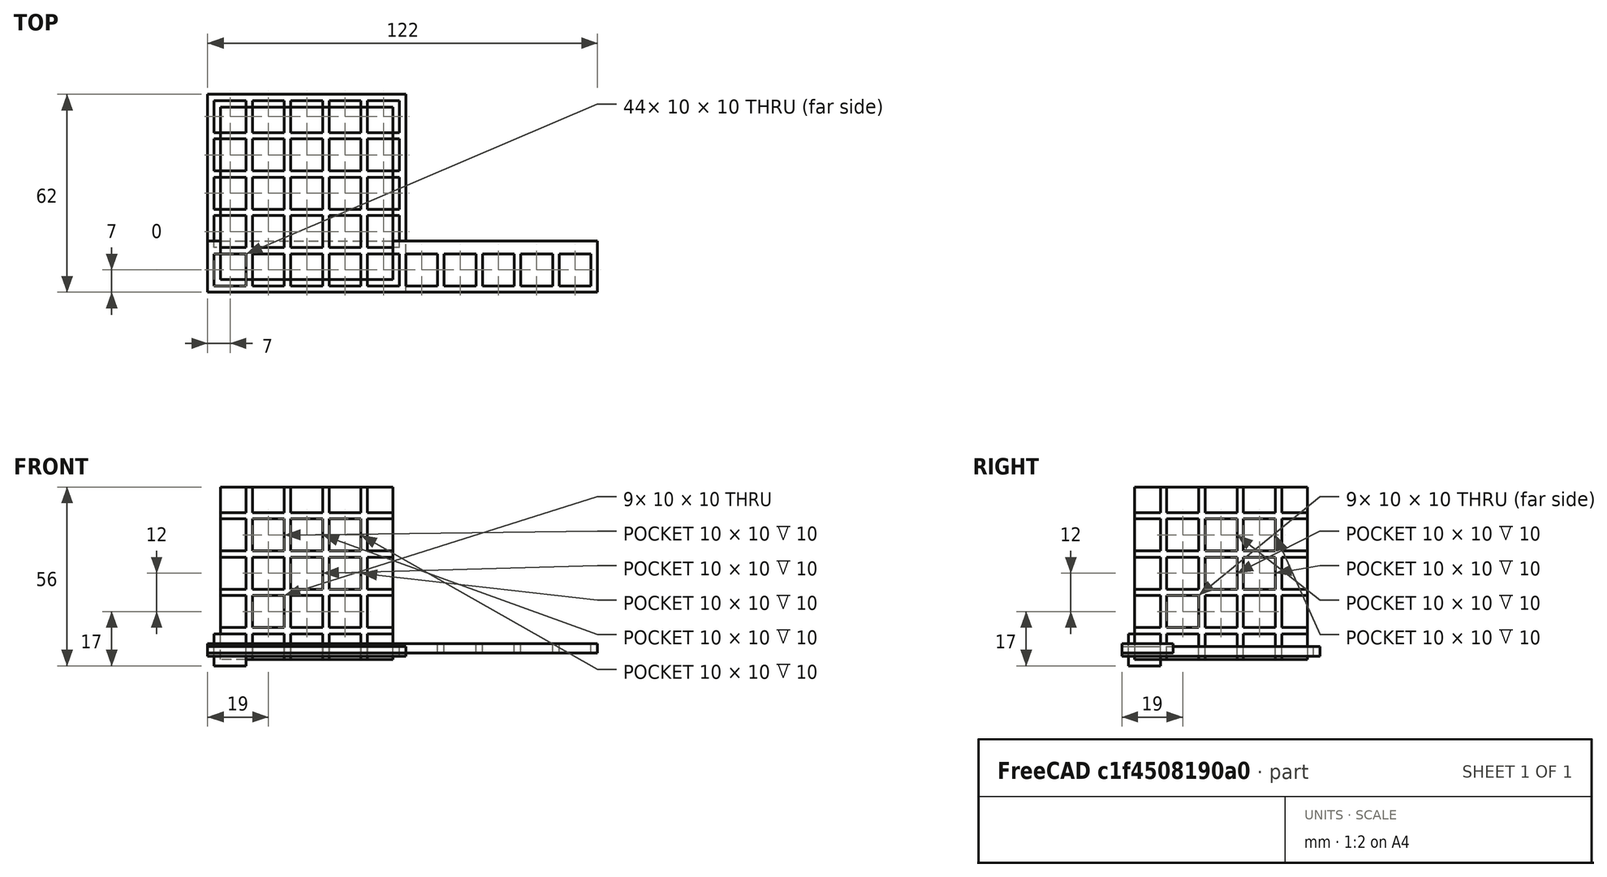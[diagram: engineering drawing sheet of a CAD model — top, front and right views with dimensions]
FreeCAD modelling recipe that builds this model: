
FCSTD DOCUMENT  (FreeCAD 0.20R29177 (Git))
Label: Video10
License: All rights reserved
LicenseURL: http://en.wikipedia.org/wiki/All_rights_reserved
objects: Part::Box×6, Part::FeaturePython×3, Part::Cut×3
note: 9 computed .brp shape members not serialized (recipe doc carries the construction recipe); baked Part::Feature solids carry a one-line shape summary decoded from their .brp

FEATURE [Part::Box] Box  label="master_box"
  AttacherType = Attacher::AttachEngine3D
  Height = 10
  Length = 10
  Width = 10
FEATURE [Part::FeaturePython] Array  # Draft array (typed FeaturePython)
  AlwaysSyncPlacement = false
  Angle = 360
  ArrayType = 0
  Axis = (0,0,1)
  Base = -> Box
  Center = (0,0,0)
  Count = 20
  ExpandArray = false
  Fuse = false
  IntervalAxis = (0,0,0)
  IntervalX = (12,0,0)
  IntervalY = (0,0,0)
  IntervalZ = (0,0,100)
  NumberCircles = 3
  NumberPolar = 5
  NumberX = 10
  NumberY = 2
  NumberZ = 1
  PlacementList = 20 placements: [(0,0,0),(0,0,0),(12,0,0),(12,0,0),(24,0,0),(24,0,0),(36,0,0),(36,0,0),(48,0,0),(48,0,0),(60,0,0),(60,0,0),(72,0,0),(72,0,0),(84,0,0),(84,0,0),(96,0,0),(96,0,0),(108,0,0),(108,0,0)]
  RadialDistance = 50
  ScaleList = (20) [(1,1,1),(1,1,1),(1,1,1),(1,1,1),(1,1,1),(1,1,1),(1,1,1),(1,1,1),(1,1,1),(1,1,1),(1,1,1),(1,1,1),(1,1,1),(1,1,1),(1,1,1),(1,1,1),(1,1,1),(1,1,1),+2 more]
  Symmetry = 1
  TangentialDistance = 25
FEATURE [Part::Box] Box001  label="Cubo"
  AttacherType = Attacher::AttachEngine3D
  Height = 3
  Length = 122
  Placement = pos=(-2,-2,4) rot=(0,0,1;0rad)
  Width = 16
FEATURE [Part::Cut] Cut
  Base = -> Box001
  Tool = -> Array
FEATURE [Part::Box] Box002  label="Cubo001"
  AttacherType = Attacher::AttachEngine3D
  Height = 10
  Length = 10
  Width = 10
FEATURE [Part::FeaturePython] Array001  # Draft array (typed FeaturePython)
  AlwaysSyncPlacement = false
  Angle = 360
  ArrayType = 0
  Axis = (0,0,1)
  Base = -> Box002
  Center = (0,0,0)
  Count = 25
  ExpandArray = false
  Fuse = false
  IntervalAxis = (0,0,0)
  IntervalX = (12,0,0)
  IntervalY = (0,12,0)
  IntervalZ = (0,0,100)
  NumberCircles = 3
  NumberPolar = 5
  NumberX = 5
  NumberY = 5
  NumberZ = 1
  PlacementList = 25 placements: [(0,0,0),(0,12,0),(0,24,0),(0,36,0),(0,48,0),(12,0,0),(12,12,0),(12,24,0),(12,36,0),(12,48,0),(24,0,0),(24,12,0),(24,24,0),(24,36,0),(24,48,0),(36,0,0),(36,12,0),(36,24,0),(36,36,0),(36,48,0),(48,0,0),(48,12,0),(48,24,0),(48,36,0),(48,48,0)]
  RadialDistance = 50
  ScaleList = (25) [(1,1,1),(1,1,1),(1,1,1),(1,1,1),(1,1,1),(1,1,1),(1,1,1),(1,1,1),(1,1,1),(1,1,1),(1,1,1),(1,1,1),(1,1,1),(1,1,1),(1,1,1),(1,1,1),(1,1,1),(1,1,1),+7 more]
  Symmetry = 1
  TangentialDistance = 25
FEATURE [Part::Box] Box003  label="Cubo002"
  AttacherType = Attacher::AttachEngine3D
  Height = 3
  Length = 62
  Placement = pos=(-2,-2,3) rot=(0,0,1;0rad)
  Width = 62
FEATURE [Part::Cut] Cut001
  Base = -> Box003
  Tool = -> Array001
FEATURE [Part::Box] Box004  label="Cubo003"
  AttacherType = Attacher::AttachEngine3D
  Height = 10
  Length = 10
  Width = 10
FEATURE [Part::FeaturePython] Array002  # Draft array (typed FeaturePython)
  AlwaysSyncPlacement = false
  Angle = 360
  ArrayType = 0
  Axis = (0,0,1)
  Base = -> Box004
  Center = (0,0,0)
  Count = 125
  ExpandArray = false
  Fuse = false
  IntervalAxis = (0,0,0)
  IntervalX = (12,0,0)
  IntervalY = (0,12,0)
  IntervalZ = (0,0,12)
  NumberCircles = 3
  NumberPolar = 5
  NumberX = 5
  NumberY = 5
  NumberZ = 5
  PlacementList = 125 placements: [(0,0,0),(0,0,12),(0,0,24),(0,0,36),(0,0,48),(0,12,0),(0,12,12),(0,12,24),(0,12,36),(0,12,48),(0,24,0),(0,24,12),(0,24,24),(0,24,36),(0,24,48),(0,36,0),(0,36,12),(0,36,24),(0,36,36),(0,36,48),(0,48,0),(0,48,12),(0,48,24),(0,48,36),(0,48,48),(12,0,0),(12,0,12),(12,0,24),(12,0,36),(12,0,48),(12,12,0),(12,12,12),(12,12,24),(12,12,36),(12,12,48),(12,24,0),(12,24,12),(12,24,24),(12,24,36),(12,24,48),+85 more]
  RadialDistance = 50
  ScaleList = (125) [(1,1,1),(1,1,1),(1,1,1),(1,1,1),(1,1,1),(1,1,1),(1,1,1),(1,1,1),(1,1,1),(1,1,1),(1,1,1),(1,1,1),(1,1,1),(1,1,1),(1,1,1),(1,1,1),(1,1,1),(1,1,1),+107 more]
  Symmetry = 1
  TangentialDistance = 25
FEATURE [Part::Box] Box005  label="Cubo004"
  AttacherType = Attacher::AttachEngine3D
  Height = 54
  Length = 54
  Placement = pos=(2,2,2) rot=(0,0,1;0rad)
  Width = 54
FEATURE [Part::Cut] Cut002
  Base = -> Box005
  Tool = -> Array002
